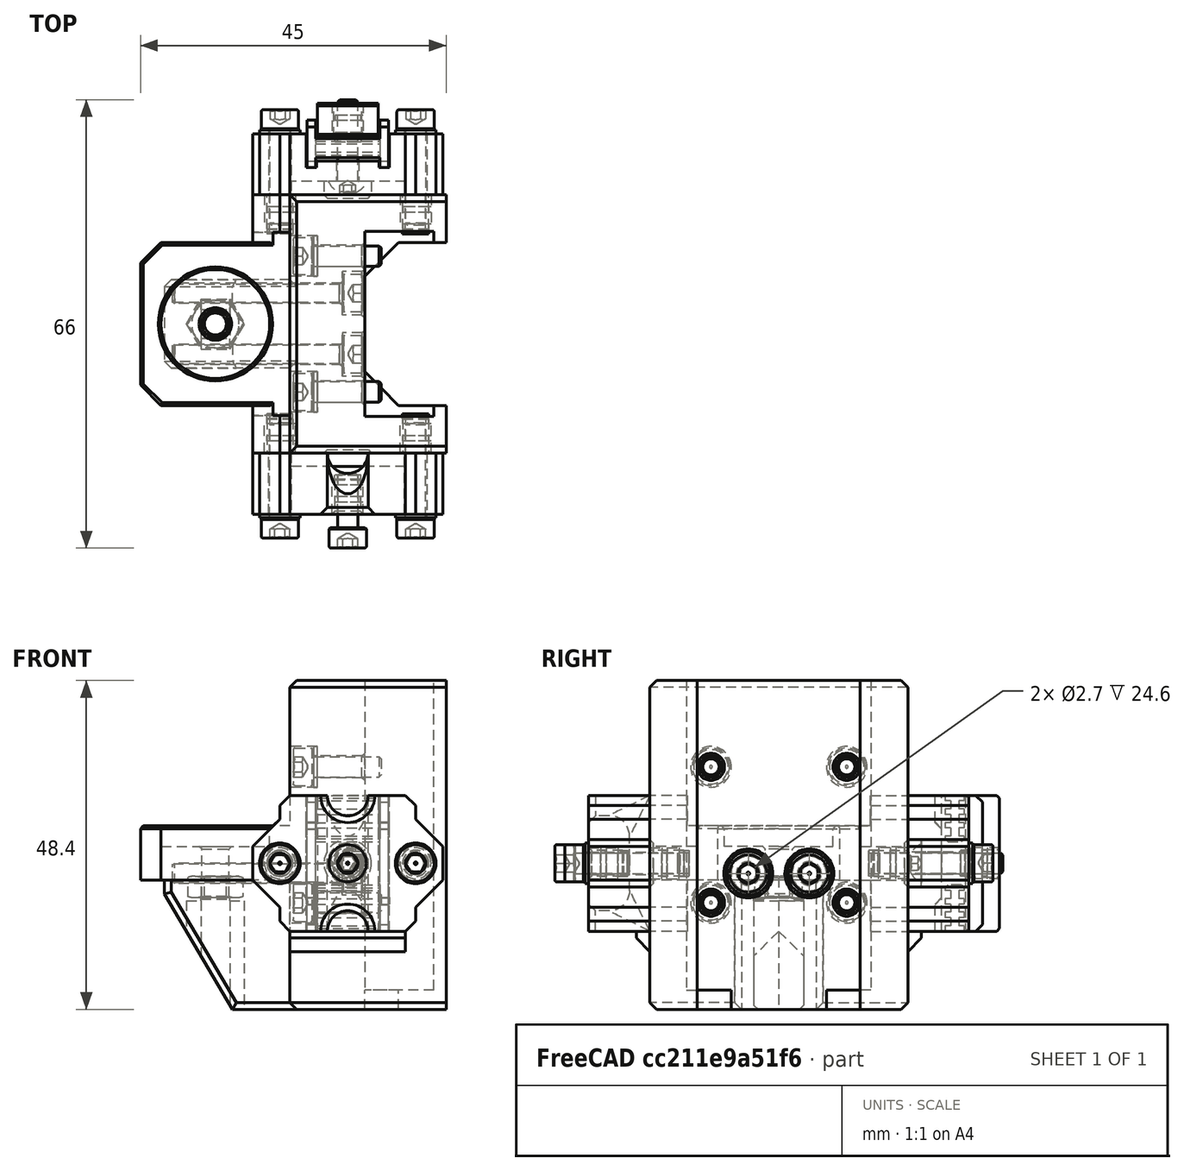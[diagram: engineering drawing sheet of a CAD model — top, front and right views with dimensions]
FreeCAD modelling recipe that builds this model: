
FCSTD DOCUMENT  (FreeCAD 0.19R24291 (Git))
Label: z-block-mount-right-counter-weight-assembly
License: Other
LicenseURL: GPL3
objects: Part::FeaturePython×27, Part::Feature×5, PartDesign::CoordinateSystem×1, App::Part×1
note: 33 computed .brp shape members not serialized (recipe doc carries the construction recipe); baked Part::Feature solids carry a one-line shape summary decoded from their .brp

FEATURE [Part::Feature] Chamfer004013007011015006002002  label="z-belt-block-mount001"
  Placement = pos=(-5,-12.5,0) rot=(0,0,1;0rad)
  shape: bbox 28 x 9 x 20 mm, 47 faces (baked)
FEATURE [Part::FeaturePython] HeatSet011  label="M3x4-HeatSet010"  # WARN: FeaturePython — macro-defined, semantics opaque (R4)
  Placement = pos=(-2.5,32.5,18.5) rot=(-1,0,0;1.5708rad)
  baseObject = -> Cut028006004005011004003001010002002004010 [Edge21]
  diameter = 2
  invert = false
  leftHanded = false
  offset = 0
FEATURE [Part::FeaturePython] Screw013  label="M3x12-Screw001"  # Fasteners workbench fastener (typed FeaturePython)
  Placement = pos=(-2.5,21,18.5) rot=(1,0,0;1.5708rad)
  baseObject = -> Chamfer004013007011015006002002 [Edge132]
  diameter = 1
  invert = false
  leftHanded = false
  length = 3
  lengthCustom = 12
  matchOuter = true
  offset = 0
  thread = false
  type = 40
FEATURE [Part::FeaturePython] Washer010  label="M3-Washer018"  # Fasteners workbench fastener (typed FeaturePython)
  Placement = pos=(7.5,28,18.5) rot=(-1,0,0;1.5708rad)
  baseObject = -> Chamfer004013007011015006002002 [Edge96]
  diameter = 4
  invert = true
  leftHanded = false
  matchOuter = true
  offset = 0
  type = 5
FEATURE [Part::FeaturePython] Washer011  label="M3-Washer019"  # Fasteners workbench fastener (typed FeaturePython)
  Placement = pos=(-12.5,28,18.5) rot=(-1,0,0;1.5708rad)
  baseObject = -> Chamfer004013007011015006002002 [Edge15]
  diameter = 4
  invert = true
  leftHanded = false
  matchOuter = true
  offset = 0
  type = 5
FEATURE [Part::FeaturePython] Screw014  label="M3x14-Screw002"  # Fasteners workbench fastener (typed FeaturePython)
  Placement = pos=(7.5,28.55,18.5) rot=(-1,0,0;1.5708rad)
  baseObject = -> Washer010 [Edge1]
  diameter = 4
  invert = false
  leftHanded = false
  length = 5
  lengthCustom = 14
  matchOuter = true
  offset = 0
  thread = false
  type = 34
FEATURE [Part::FeaturePython] Screw015  label="M3x14-Screw003"  # Fasteners workbench fastener (typed FeaturePython)
  Placement = pos=(-12.5,28.55,18.5) rot=(-1,0,0;1.5708rad)
  baseObject = -> Washer011 [Edge1]
  diameter = 4
  invert = false
  leftHanded = false
  length = 5
  lengthCustom = 14
  matchOuter = true
  offset = 0
  thread = false
  type = 34
FEATURE [Part::Feature] Cut028006004005011004003001010002002004009  label="z-belt-mounter-middle001"
  Placement = pos=(-5,-14,0) rot=(0,0,1;0rad)
  shape: bbox 12 x 7 x 20 mm, 80 faces (baked)
FEATURE [Part::Feature] Cut028006004005011004003001010002002004010  label="z-belt-mounter-clamp-nut001"
  Placement = pos=(-2.5,36,18.5) rot=(-1,0,0;1.5708rad)
  shape: bbox 9 x 5 x 20 mm, 11 faces (baked)
FEATURE [PartDesign::CoordinateSystem] LCS_z_rail_block_mount_x_slider  label="LCS_z-rail-block-mount-x-slider-counter-weight"
  AttacherType = Attacher::AttachEngine3D
FEATURE [Part::FeaturePython] Washer006  label="M3-Washer"  # Fasteners workbench fastener (typed FeaturePython)
  Placement = pos=(-7,10,12.7) rot=(0,-1,0;1.5708rad)
  diameter = 4
  invert = true
  leftHanded = false
  matchOuter = true
  offset = 0
  type = 5
FEATURE [Part::FeaturePython] Washer007  label="M3-Washer020"  # Fasteners workbench fastener (typed FeaturePython)
  Placement = pos=(-7,10,32.7) rot=(0,-1,0;1.5708rad)
  diameter = 4
  invert = true
  leftHanded = false
  matchOuter = true
  offset = 0
  type = 5
FEATURE [Part::FeaturePython] Washer008  label="M3-Washer021"  # Fasteners workbench fastener (typed FeaturePython)
  Placement = pos=(-7,-10,32.7) rot=(0,-1,0;1.5708rad)
  diameter = 4
  invert = true
  leftHanded = false
  matchOuter = true
  offset = 0
  type = 5
FEATURE [Part::FeaturePython] Washer009  label="M3-Washer022"  # Fasteners workbench fastener (typed FeaturePython)
  Placement = pos=(-7,-10,12.7) rot=(0,-1,0;1.5708rad)
  diameter = 4
  invert = true
  leftHanded = false
  matchOuter = true
  offset = 0
  type = 5
FEATURE [Part::FeaturePython] Screw009  label="M3x10-Screw"  # Fasteners workbench fastener (typed FeaturePython)
  Placement = pos=(-7.55,10,12.7) rot=(0,-1,0;1.5708rad)
  baseObject = -> Washer006 [Edge1]
  diameter = 4
  invert = false
  leftHanded = false
  length = 3
  lengthCustom = 10
  matchOuter = true
  offset = 0
  thread = false
  type = 34
FEATURE [Part::FeaturePython] Screw010  label="M3x10-Screw004"  # Fasteners workbench fastener (typed FeaturePython)
  Placement = pos=(-7.55,10,32.7) rot=(0,-1,0;1.5708rad)
  baseObject = -> Washer007 [Edge1]
  diameter = 4
  invert = false
  leftHanded = false
  length = 3
  lengthCustom = 10
  matchOuter = true
  offset = 0
  thread = false
  type = 34
FEATURE [Part::FeaturePython] Screw011  label="M3x10-Screw005"  # Fasteners workbench fastener (typed FeaturePython)
  Placement = pos=(-7.55,-10,32.7) rot=(0,-1,0;1.5708rad)
  baseObject = -> Washer008 [Edge1]
  diameter = 4
  invert = false
  leftHanded = false
  length = 3
  lengthCustom = 10
  matchOuter = true
  offset = 0
  thread = false
  type = 34
FEATURE [Part::FeaturePython] Screw012  label="M3x10-Screw006"  # Fasteners workbench fastener (typed FeaturePython)
  Placement = pos=(-7.55,-10,12.7) rot=(0,-1,0;1.5708rad)
  baseObject = -> Washer009 [Edge1]
  diameter = 4
  invert = false
  leftHanded = false
  length = 3
  lengthCustom = 10
  matchOuter = true
  offset = 0
  thread = false
  type = 34
FEATURE [Part::FeaturePython] HeatSet007  label="M3x4-HeatSet006"  # WARN: FeaturePython — macro-defined, semantics opaque (R4)
  Placement = pos=(7.5,19,18.5) rot=(-1,0,0;1.5708rad)
  diameter = 2
  invert = true
  leftHanded = false
  offset = 0
FEATURE [Part::FeaturePython] HeatSet008  label="M3x4-HeatSet007"  # WARN: FeaturePython — macro-defined, semantics opaque (R4)
  Placement = pos=(-12.5,19,18.5) rot=(-1,0,0;1.5708rad)
  diameter = 2
  invert = true
  leftHanded = false
  offset = 0
FEATURE [Part::FeaturePython] HeatSet  label="M3x4-HeatSet"  # WARN: FeaturePython — macro-defined, semantics opaque (R4)
  Placement = pos=(-12.5,-19,18.5) rot=(1,0,0;1.5708rad)
  diameter = 2
  invert = false
  leftHanded = false
  offset = 0
FEATURE [Part::FeaturePython] HeatSet012  label="M3x4-HeatSet001"  # WARN: FeaturePython — macro-defined, semantics opaque (R4)
  Placement = pos=(7.5,-19,18.5) rot=(1,0,0;1.5708rad)
  diameter = 2
  invert = false
  leftHanded = false
  offset = 0
FEATURE [Part::Feature] Chamfer026018001001  label="wire-mounter002"
  Placement = pos=(-2.5,-19,18.5) rot=(1,0,0;1.5708rad)
  shape: bbox 28 x 9 x 20 mm, 41 faces (baked)
FEATURE [Part::FeaturePython] Washer  label="M3-Washer025"  # Fasteners workbench fastener (typed FeaturePython)
  Placement = pos=(-12.5,-28,18.5) rot=(1,0,0;1.5708rad)
  baseObject = -> Chamfer026018001001 [Edge101]
  diameter = 4
  invert = true
  leftHanded = false
  matchOuter = true
  offset = 0
  type = 5
FEATURE [Part::FeaturePython] Washer012  label="M3-Washer026"  # Fasteners workbench fastener (typed FeaturePython)
  Placement = pos=(7.5,-28,18.5) rot=(1,0,0;1.5708rad)
  baseObject = -> Chamfer026018001001 [Edge100]
  diameter = 4
  invert = true
  leftHanded = false
  matchOuter = true
  offset = 0
  type = 5
FEATURE [Part::FeaturePython] Screw  label="M3x14-Screw"  # Fasteners workbench fastener (typed FeaturePython)
  Placement = pos=(-12.5,-28.55,18.5) rot=(1,0,0;1.5708rad)
  baseObject = -> Washer [Edge1]
  diameter = 4
  invert = false
  leftHanded = false
  length = 5
  lengthCustom = 14
  matchOuter = true
  offset = 0
  thread = false
  type = 34
FEATURE [Part::FeaturePython] Screw019  label="M3x14-Screw004"  # Fasteners workbench fastener (typed FeaturePython)
  Placement = pos=(7.5,-28.55,18.5) rot=(1,0,0;1.5708rad)
  baseObject = -> Washer012 [Edge1]
  diameter = 4
  invert = false
  leftHanded = false
  length = 5
  lengthCustom = 14
  matchOuter = true
  offset = 0
  thread = false
  type = 34
FEATURE [Part::FeaturePython] HeatSet013  label="M3-HeatSet"  # WARN: FeaturePython — macro-defined, semantics opaque (R4)
  Placement = pos=(-2.5,-28,18.5) rot=(1,0,0;1.5708rad)
  baseObject = -> Chamfer026018001001 [Edge99]
  diameter = 2
  invert = false
  leftHanded = false
  offset = 0
FEATURE [Part::FeaturePython] Screw020  label="M3x8-Screw"  # Fasteners workbench fastener (typed FeaturePython)
  Placement = pos=(-2.5,-30,18.5) rot=(1,0,0;1.5708rad)
  baseObject = -> HeatSet013 [Edge1]
  diameter = 4
  invert = false
  leftHanded = false
  length = 2
  lengthCustom = 8
  matchOuter = true
  offset = 2
  thread = false
  type = 34
FEATURE [Part::Feature] Fusion004025023004001002001  label="z-rail-block-mount-right-counter-weight"
  Placement = pos=(0,0,0) rot=(0,0,1;3.14159rad)
  shape: bbox 45 x 42 x 48.4 mm, 139 faces (baked)
FEATURE [Part::FeaturePython] Screw021  label="M3x25-Screw"  # Fasteners workbench fastener (typed FeaturePython)
  Placement = pos=(-3.3,-4.5,17) rot=(0,1,0;1.5708rad)
  baseObject = -> Fusion004025023004001002001 [Edge301]
  diameter = 4
  invert = true
  leftHanded = false
  length = 8
  lengthCustom = 25
  matchOuter = true
  offset = 0
  thread = false
  type = 36
FEATURE [Part::FeaturePython] Screw022  label="M3x25-Screw001"  # Fasteners workbench fastener (typed FeaturePython)
  Placement = pos=(-3.3,4.5,17) rot=(0,1,0;1.5708rad)
  baseObject = -> Fusion004025023004001002001 [Edge310]
  diameter = 4
  invert = false
  leftHanded = false
  length = 8
  lengthCustom = 25
  matchOuter = true
  offset = 0
  thread = false
  type = 36
FEATURE [Part::FeaturePython] Nut  label="M4-Nut"  # Fasteners workbench fastener (typed FeaturePython)
  Placement = pos=(-22,2.7e-15,13.4) rot=(0,0,1;0rad)
  baseObject = -> Fusion004025023004001002001 [Edge33]
  diameter = 6
  invert = false
  leftHanded = false
  matchOuter = true
  offset = 0
  thread = false
  type = 9
FEATURE [App::Part] Part001  label="z-rail-block-mount-x-slider-counter-weight"
  Group = -> [Cut028006004005011004003001010002002004010,Cut028006004005011004003001010002002004009,Chamfer004013007011015006002002,Washer006,Washer007,Washer008,Washer009,Screw009,Screw010,Screw011,Screw012,HeatSet007,HeatSet008,HeatSet011,Screw013,Washer010,Washer011,Screw014,Screw015,LCS_z_rail_block_mount_x_slider,HeatSet,HeatSet012,Chamfer026018001001,Washer,Washer012,Screw,Screw019,HeatSet013,Screw020,+4 more]
  Origin = -> Origin001
